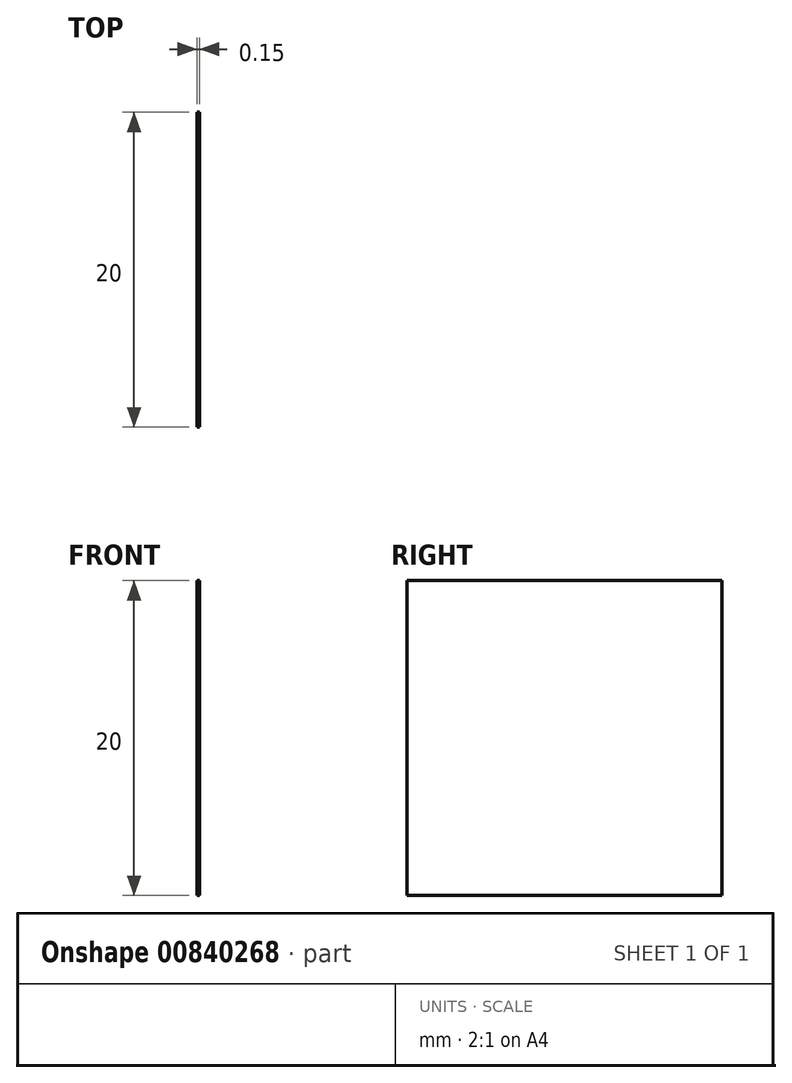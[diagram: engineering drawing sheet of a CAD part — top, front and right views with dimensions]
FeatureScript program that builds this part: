
annotation { "Feature Type Name" : "Feature", "Feature Type Description" : "" }
export const myFeature = defineFeature(function(context is Context, id is Id, definition is map)
    precondition{}
    {
        {
            var Q0;
            Q0=qCreatedBy(makeId("Right.planeOp"),FACE);
            var sketch = newSketch(context, id + "F0", { "sketchPlane" : qUnion([Q0])});
            skLineSegment(sketch, "E0.bottom", {"start": v(0, 0) * mm, "end": v(20, 0) * mm});
            skLineSegment(sketch, "E0.top", {"start": v(0, -20) * mm, "end": v(20, -20) * mm});
            skLineSegment(sketch, "E0.left", {"start": v(0, 0) * mm, "end": v(0, -20) * mm});
            skLineSegment(sketch, "E0.right", {"start": v(20, 0) * mm, "end": v(20, -20) * mm});
            skSolve(sketch);
        }
        {
            var Q0;
            Q0=makeQuery(id+"F0.imprint","IMPRINT",FACE,{"disambiguationData":[TD([[makeQuery(id+"F0.imprint","IMPRINT",EDGE,{"derivedFrom":sQuery(id+"F0.wireOp",EDGE,"E0.bottom")}),-1.0]])]});
            extrude(context, id + "F1", {"entities" : qUnion([Q0]), "depth" : .15 * mm, "offsetDistance" : 25 * mm});
        }
    });
